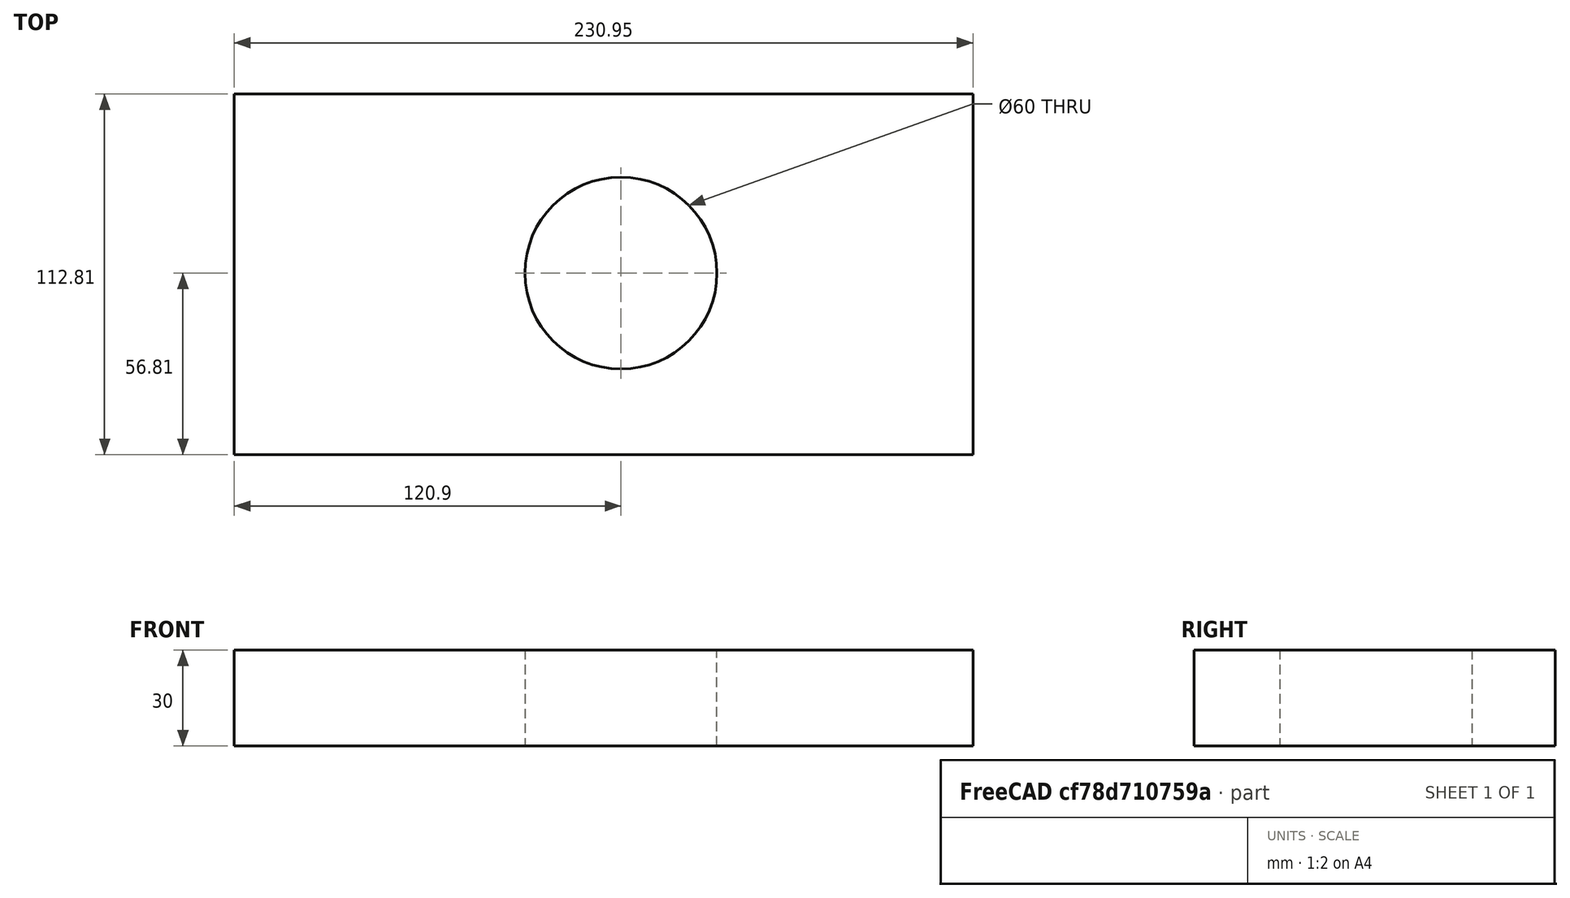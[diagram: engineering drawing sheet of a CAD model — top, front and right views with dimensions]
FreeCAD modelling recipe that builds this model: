
FCSTD DOCUMENT  (FreeCAD 0.16RUnknown)
Label: Block
License: All rights reserved
LicenseURL: http://en.wikipedia.org/wiki/All_rights_reserved
objects: Fem::FemResultObject×6, Fem::ConstraintHeatflux×2, Sketcher::SketchObject×1, PartDesign::Pad×1, Fem::FemSolverObjectPython×1, Fem::FemMeshShapeNetgenObject×1, App::MaterialObjectPython×1, Fem::ConstraintDisplacement×1, Fem::ConstraintFixed×1, Fem::ConstraintInitialTemperature×1, Fem::FemAnalysisPython×1
note: 3 computed .brp shape members not serialized (recipe doc carries the construction recipe); baked Part::Feature solids carry a one-line shape summary decoded from their .brp

FEATURE [Sketcher::SketchObject] Sketch
  sketch-geometry (5):
    g0: LineSegment StartX=-120.897 StartY=-56.8143 StartZ=0 EndX=110.046 EndY=-56.8143 EndZ=0
    g1: LineSegment StartX=110.046 StartY=-56.8143 StartZ=0 EndX=110.046 EndY=56 EndZ=0
    g2: LineSegment StartX=110.046 StartY=56 StartZ=0 EndX=-120.897 EndY=56 EndZ=0
    g3: LineSegment StartX=-120.897 StartY=56 StartZ=0 EndX=-120.897 EndY=-56.8143 EndZ=0
    g4: Circle CenterX=0 CenterY=0 CenterZ=0 NormalX=0 NormalY=0 NormalZ=1 Radius=30
  constraints (10):
    c: Coincident(g0,g1)
    c: Coincident(g1,g2)
    c: Coincident(g2,g3)
    c: Coincident(g3,g0)
    c: Horizontal(g0)
    c: Horizontal(g2)
    c: Vertical(g1)
    c: Vertical(g3)
    c: Coincident(g4,g-1)
    c: Radius(g4) = 30
FEATURE [PartDesign::Pad] Pad
  Length = 30
  Length2 = 100
  Sketch = -> Sketch
  Type = 0
FEATURE [Fem::FemSolverObjectPython] CalculiX  # FEM object (typed FeaturePython)
  AnalysisType = 2
  EigenmodeHighLimit = 1000000
  EigenmodeLowLimit = 0
  EndTime = 10
  InitialTimeStep = 1
  MatrixSolverType = 0
  Maxiterations = 2000
  NonLinearGeometry = false
  NumCpus = 3
  NumberOfEigenmodes = 10
  SolverType = FemSolverCalculix
  SteadyState = false
FEATURE [Fem::FemMeshShapeNetgenObject] Pad_Mesh
  Fineness = 3
  GrowthRate = 0.3
  MaxSize = 1000
  NbSegsPerEdge = 1
  NbSegsPerRadius = 2
  Optimize = true
  SecondOrder = true
  Shape = -> Pad
FEATURE [App::MaterialObjectPython] MechanicalMaterial  # material (typed FeaturePython)
  Material = Density=7900.0 kg/m^3,Description=Standard steel material for CalculiX sample calculations,Father=Metal,Name=CalculiX-Steel,PoissonRatio=0.3,+4 more (map truncated)
FEATURE [Fem::ConstraintDisplacement] FemConstraintDisplacement
  NormalDirection = (1,0,0)
  Normals = (32) [(1,0,0),(1,0,0),(1,0,0),(1,0,0),(1,0,0),(1,0,0),(1,0,0),(1,0,0),(1,0,0),(1,0,0),(1,0,0),(1,0,0),(1,0,0),(1,0,0),(1,0,0),(1,0,0),(-1,0,0),(-1,0,0),+14 more]
  Points = (32) [(110.046,-56.8143,30),(110.046,-19.2095,30),(110.046,18.3952,30),(110.046,56,30),(110.046,-56.8143,20),(110.046,-19.2095,20),(110.046,18.3952,20),+25 more]
  References = -> [Pad]
  Scale = 8
  rotxFix = false
  rotxFree = true
  rotyFix = false
  rotyFree = true
  rotzFix = false
  rotzFree = true
  xDisplacement = 0
  xFix = true
  xFree = false
  xRotation = 0
  yDisplacement = 0
  yFix = false
  yFree = true
  yRotation = 0
  zDisplacement = 0
  zFix = false
  zFree = true
  zRotation = 0
FEATURE [Fem::ConstraintFixed] FemConstraintFixed
  NormalDirection = (0,0,1)
  Normals = (1) [(0,0,1)]
  Points = (1) [(-120.897,56,30)]
  References = -> [Pad]
  Scale = 22
FEATURE [Fem::ConstraintHeatflux] FemConstraintHeatflux
  AmbientTemp = 300
  FilmCoef = 10
  NormalDirection = (-1,0,0)
  Normals = (16) [(-1,0,0),(-1,0,0),(-1,0,0),(-1,0,0),(-1,0,0),(-1,0,0),(-1,0,0),(-1,0,0),(-1,0,0),(-1,0,0),(-1,0,0),(-1,0,0),(-1,0,0),(-1,0,0),(-1,0,0),(-1,0,0)]
  Points = (16) [(-120.897,56,30),(-120.897,18.3952,30),(-120.897,-19.2095,30),(-120.897,-56.8143,30),(-120.897,56,20),(-120.897,18.3952,20),(-120.897,-19.2095,20),+9 more]
  References = -> [Pad]
  Scale = 8
FEATURE [Fem::ConstraintHeatflux] FemConstraintHeatflux001
  AmbientTemp = 900
  FilmCoef = 10
  NormalDirection = (1,0,0)
  Normals = (16) [(1,0,0),(1,0,0),(1,0,0),(1,0,0),(1,0,0),(1,0,0),(1,0,0),(1,0,0),(1,0,0),(1,0,0),(1,0,0),(1,0,0),(1,0,0),(1,0,0),(1,0,0),(1,0,0)]
  Points = (16) [(110.046,-56.8143,30),(110.046,-19.2095,30),(110.046,18.3952,30),(110.046,56,30),(110.046,-56.8143,20),(110.046,-19.2095,20),(110.046,18.3952,20),+9 more]
  References = -> [Pad]
  Scale = 8
FEATURE [Fem::ConstraintInitialTemperature] FemConstraintInitialTemperature
  NormalDirection = (0,0,1)
  initialTemperature = 300
FEATURE [Fem::FemResultObject] Time_1_0_results
  DisplacementLengths = [1.09043e-05,1.08621e-05,0,4.79698e-07,7.0179e-05,6.99295e-05,7.0611e-05,7.07108e-05,1.40134e-06,1.47478e-06,1.62896e-06,2.35189e-06,3.74579e-06,5.73156e-06,7.41138e-06,8.4937e-06,9.504e-06,1.14327e-05,1.50741e-05,2.118e-05,3.08816e-05,+1831 more]
  DisplacementVectors = (1852) [(-1.08695e-05,-8.70105e-07,-1.09746e-08),(-1.08346e-05,-7.69694e-07,-6.22541e-08),(0,0,0),(0,-1.00836e-08,-4.79592e-07),(0,6.18968e-05,3.30739e-05),+1847 more]
  Eigenmode = 0
  EigenmodeFrequency = 0
  MaxShear = [0.00110132,0.00145114,0.0056175,0.00559389,0.684787,0.707023,0.686506,0.593066,0.00568351,0.00566764,0.00585237,0.00650454,0.00787853,0.0090864,0.00818334,0.0068105,0.0104173,0.0157375,0.0224242,0.0399391,0.171137,0.282705,0.478545,+1829 more]
  Mesh = -> Pad_Mesh
  NodeNumbers = [1,2,3,4,5,6,7,8,9,10,11,12,13,14,15,16,17,18,19,20,21,22,23,24,25,26,27,28,29,30,31,32,33,34,35,36,37,38,39,40,41,42,43,44,45,46,47,48,49,50,51,52,53,54,55,56,57,58,59,60,61,62,63,64,65,66,67,68,69,+1783 more]
  PrincipalMax = [-5.90334e-05,0.000101181,2.19898e-05,1.62717e-05,0.850149,0.899198,0.870237,0.699655,1.6515e-05,1.54824e-05,4.15293e-05,7.79948e-05,1.57775e-05,6.37336e-05,0.000426934,0.000181857,0.00042271,0.00092082,0.00510631,0.0555829,0.198626,+1831 more]
  PrincipalMed = [-0.000244752,-0.000154764,-2.78992e-06,-3.12636e-06,0.113433,0.11918,0.0859452,0.143449,-9.03912e-06,-9.49593e-06,5.954e-06,-6.84071e-05,-6.32103e-05,-0.000156076,-0.000207615,-5.34835e-05,-0.000185036,-0.000129886,0.000802053,0.0283716,+1832 more]
  PrincipalMin = [-0.00226167,-0.00280111,-0.011213,-0.0111715,-0.519425,-0.514849,-0.502774,-0.486478,-0.0113505,-0.0113198,-0.0116632,-0.0129311,-0.0157413,-0.0181091,-0.0159397,-0.0134391,-0.0204118,-0.0305542,-0.039742,-0.0242954,-0.143649,-0.491018,+1830 more]
  Stats = [-4.08679e-05,-7.69615e-06,0,-6.38528e-05,-1.00231e-06,6.32438e-05,-4.62787e-05,-1.86336e-07,4.69683e-05,0,9.60651e-06,7.07108e-05,0.000599773,0.0453101,1.22677,-0.418726,0.0135637,0.899198,-0.615163,-0.00228516,0.40572,-1.071,-0.0358433,+4 more]
  StressValues = [0.0021159,0.00278316,0.0112226,0.0111781,1.18722,1.22677,1.19308,1.02788,0.0113543,0.0113228,0.011687,0.0129365,0.0157177,0.0180639,0.0160588,0.0135049,0.0205374,0.030963,0.0428586,0.0703377,0.316557,0.537739,0.876323,0.88264,0.764111,+1827 more]
  Temperature = [300,300,300,300,300.434,300.436,300.432,300.392,300,300,300,300,300,300,300,300,300,300,300.003,300.01,300.089,300.345,300.387,300.386,300.376,300.333,300.1,300.019,300.002,300,300,300,300,300,300,300,300,300,300,300,300,300,300,300,300,+1807 more]
  Time = 1
FEATURE [Fem::FemResultObject] Time_2_0_results
  DisplacementLengths = [2.18488e-05,2.17538e-05,0,9.58297e-07,0.00012698,0.000126633,0.000128639,0.000130319,2.79994e-06,2.95303e-06,3.25509e-06,4.70093e-06,7.48937e-06,1.14626e-05,1.48243e-05,1.699e-05,1.90122e-05,2.29244e-05,3.05133e-05,4.3104e-05,6.62821e-05,+1831 more]
  DisplacementVectors = (1852) [(-2.17801e-05,-1.72959e-06,-6.08378e-08),(-2.16977e-05,-1.55197e-06,-1.69272e-07),(0,0,0),(0,2.15053e-09,-9.58295e-07),(0,0.000113029,5.78647e-05),+1847 more]
  Eigenmode = 0
  EigenmodeFrequency = 0
  MaxShear = [0.00225657,0.00283529,0.011228,0.0111741,1.05466,1.08635,1.0603,0.939602,0.011367,0.0113247,0.0117052,0.0130111,0.0157637,0.0181787,0.0163653,0.0136216,0.0208272,0.0311753,0.0420788,0.0655236,0.231569,0.4507,0.762146,0.778937,0.649304,+1827 more]
  Mesh = -> Pad_Mesh
  NodeNumbers = <same value as first occurrence — deduplicated (x6 in doc)>
  PrincipalMax = [-0.000207255,-3.28875e-05,4.40388e-05,3.25091e-05,1.39256,1.46814,1.43479,1.19114,3.31754e-05,3.08608e-05,8.34441e-05,0.000156825,3.42952e-05,0.00012231,0.000834106,0.000354707,0.000795803,0.00104202,0.00463659,0.0547592,0.283085,0.115979,+1830 more]
  PrincipalMed = [-0.00050751,-0.000641127,-5.56256e-06,-6.27033e-06,0.159591,0.165646,0.129627,0.223159,-1.81605e-05,-1.89519e-05,1.16287e-05,-0.000138075,-0.000129735,-0.000307637,-0.000401744,-0.000107818,-0.000390272,-0.000665803,-0.00143959,0.0240729,+1832 more]
  PrincipalMin = [-0.00472039,-0.00570347,-0.0224119,-0.0223156,-0.716762,-0.704556,-0.685819,-0.68806,-0.0227009,-0.0226186,-0.023327,-0.0258654,-0.0314931,-0.0362351,-0.0318964,-0.0268885,-0.0408586,-0.0613086,-0.0795209,-0.076288,-0.180053,-0.785422,+1830 more]
  Stats = [-7.10932e-05,-1.53471e-05,0,-0.000117327,-2.00347e-06,0.00011511,-7.99931e-05,-3.91939e-07,8.11663e-05,0,1.89832e-05,0.000130319,0.0011333,0.0788371,1.89398,-0.638307,0.0235823,1.46814,-0.867213,-0.00397535,0.555405,-1.59213,-0.0621923,+4 more]
  StressValues = [0.00437075,0.00539225,0.0224312,0.0223288,1.83541,1.89398,1.85275,1.62769,0.0227085,0.0226246,0.0233746,0.0258761,0.0314457,0.0361443,0.0321304,0.0270149,0.0410742,0.0615145,0.0812899,0.118717,0.443666,0.846769,1.38725,1.42239,1.25009,+1827 more]
  Temperature = [300,300,300,300,300.664,300.665,300.661,300.618,300,300,300,300,300,300,300,300,300,300,299.999,300.001,300.057,300.569,300.614,300.616,300.607,300.553,300.068,300.003,299.999,300,300,300,300,300,300,300,300,300,300,300,300,300,300,300,300,+1807 more]
  Time = 2
FEATURE [Fem::FemResultObject] Time_3_5_results
  DisplacementLengths = [3.82841e-05,3.80991e-05,0,1.67626e-06,0.00019983,0.000199569,0.000203916,0.000207684,4.89388e-06,5.17074e-06,5.6904e-06,8.22084e-06,1.31021e-05,2.00591e-05,2.59483e-05,2.97453e-05,3.32894e-05,4.01404e-05,5.35684e-05,7.59911e-05,0.000121233,+1831 more]
  DisplacementVectors = (1852) [(-3.81667e-05,-2.9858e-06,-2.44551e-07),(-3.79979e-05,-2.74557e-06,-4.05729e-07),(0,0,0),(0,2.7475e-08,-1.67603e-06),(0,0.000180082,8.66172e-05),+1847 more]
  Eigenmode = 0
  EigenmodeFrequency = 0
  MaxShear = [0.0037116,0.00436665,0.0196363,0.0195444,1.41245,1.45008,1.42233,1.27219,0.0198882,0.0198095,0.0204815,0.0227719,0.0276033,0.0318338,0.0286527,0.023875,0.036521,0.0545377,0.0714299,0.100265,0.265172,0.603492,1.03013,1.06827,0.902574,+1827 more]
  Mesh = -> Pad_Mesh
  NodeNumbers = <same value as first occurrence — deduplicated (x6 in doc)>
  PrincipalMax = [-0.000344131,-8.16902e-06,7.73031e-05,5.68076e-05,1.99012,2.08498,2.04847,1.73146,5.845e-05,5.37905e-05,0.000147109,0.000276887,6.76441e-05,0.000202598,0.00141284,0.00061469,0.00144529,0.00141561,0.00350054,0.033374,0.356381,0.160158,+1830 more]
  PrincipalMed = [-0.000766111,-0.000807176,-9.72986e-06,-1.10015e-05,0.201287,0.206745,0.169951,0.293053,-3.19918e-05,-3.31021e-05,1.97018e-05,-0.000244848,-0.000235252,-0.000527882,-0.000669585,-0.000179093,-0.000721412,-0.00141902,-0.00458846,0.00453159,+1832 more]
  PrincipalMin = [-0.00776734,-0.00874148,-0.0391952,-0.039032,-0.834772,-0.815179,-0.796195,-0.812919,-0.039718,-0.0395652,-0.0408159,-0.0452669,-0.055139,-0.063465,-0.0558926,-0.0471353,-0.0715966,-0.10766,-0.139359,-0.167155,-0.173964,-1.04683,-1.69697,+1829 more]
  Stats = [-0.000106681,-2.67022e-05,0,-0.000188601,-3.50341e-06,0.00018259,-0.000119388,-7.37648e-07,0.000120714,0,3.27623e-05,0.000207684,0.00205536,0.119705,2.54785,-0.855803,0.0358909,2.08498,-1.04622,-0.00577115,0.670129,-2.07371,-0.0939302,+4 more]
  StressValues = [0.00722147,0.00836248,0.0392291,0.039055,2.47522,2.54785,2.50544,2.20976,0.0397313,0.0395756,0.0408995,0.0452851,0.0550559,0.0633055,0.0562931,0.0473581,0.071983,0.107686,0.138992,0.187777,0.513387,1.123,1.85958,1.93456,1.71317,1.09877,+1826 more]
  Temperature = [300,300,300,300,300.893,300.892,300.888,300.85,300,300,300,300,300,300,300,300,300,300,299.999,300,300.044,300.813,300.854,300.857,300.854,300.793,300.045,299.997,300,300,300,300,300,300,300,300,300,300,300,300,300,300,300,300,300,300,300,+1805 more]
  Time = 3.5
FEATURE [Fem::FemResultObject] Time_5_75_results
  DisplacementLengths = [6.29388e-05,6.26481e-05,0,2.75319e-06,0.000295664,0.000295775,0.000303523,0.000309661,8.02308e-06,8.48605e-06,9.33281e-06,1.34925e-05,2.15168e-05,3.29572e-05,4.26502e-05,4.89126e-05,5.47621e-05,6.60506e-05,8.82128e-05,0.000125487,+1832 more]
  DisplacementVectors = (1852) [(-6.27502e-05,-4.82071e-06,-6.80176e-07),(-6.24757e-05,-4.5684e-06,-8.40499e-07),(0,0,0),(0,5.25656e-08,-2.75269e-06),(0,0.000269929,0.000120646),+1847 more]
  Eigenmode = 0
  EigenmodeFrequency = 0
  MaxShear = [0.00498814,0.00564238,0.0322382,0.0321117,1.77884,1.81776,1.79023,1.60584,0.0326599,0.0325431,0.0336379,0.0374129,0.0453845,0.0523584,0.0471379,0.0393402,0.0601682,0.0898015,0.115688,0.16351,0.294004,0.744185,1.28713,1.35096,1.15258,+1827 more]
  Mesh = -> Pad_Mesh
  NodeNumbers = <same value as first occurrence — deduplicated (x6 in doc)>
  PrincipalMax = [-0.000468741,0.000118146,0.000127563,9.32511e-05,2.651,2.75481,2.71662,2.32596,9.6769e-05,8.81154e-05,0.000243742,0.000459558,0.000124778,0.000316176,0.00224616,0.00100294,0.00246665,0.00225985,0.00332778,0.0228985,0.456309,0.212873,+1830 more]
  PrincipalMed = [-0.00112323,-0.00103213,-1.59929e-05,-1.81313e-05,0.23893,0.242939,0.204965,0.356864,-5.29564e-05,-5.43427e-05,3.13426e-05,-0.000407813,-0.00039981,-0.000852137,-0.00104902,-0.000289348,-0.00122757,-0.00212086,-0.00788058,-0.0333792,+1832 more]
  PrincipalMin = [-0.010445,-0.0111666,-0.0643488,-0.0641301,-0.906686,-0.880708,-0.863835,-0.885721,-0.065223,-0.064998,-0.0670321,-0.0743663,-0.0906443,-0.104401,-0.0920296,-0.0776776,-0.11787,-0.177343,-0.228048,-0.304121,-0.1317,-1.2755,-2.06136,-2.1775,+1828 more]
  Stats = [-0.000155816,-4.35177e-05,0,-0.000284258,-5.75221e-06,0.000272135,-0.000167088,-1.30359e-06,0.00016798,0,5.30334e-05,0.000309661,0.00317547,0.171848,3.22406,-1.09336,0.0513149,2.75481,-1.22538,-0.00791231,0.765987,-2.53874,-0.13432,+4 more]
  StressValues = [0.00966568,0.0107559,0.0644047,0.0641678,3.14545,3.22406,3.18358,2.80501,0.0652451,0.065015,0.0671699,0.074396,0.0905079,0.104138,0.0926721,0.0780424,0.118532,0.177453,0.22598,0.302829,0.541282,1.37578,2.30545,2.42831,2.15622,1.35925,+1826 more]
  Temperature = [300,300,300,300,301.14,301.139,301.134,301.106,300,300,300,300,300,300,300,300,300,300,300,300.005,300.081,301.08,301.113,301.117,301.118,301.062,300.066,300.001,300,300,300,300,300,300,300,300,300,300,300,300,300,300,300,300,300,300,300,+1805 more]
  Time = 5.75
FEATURE [Fem::FemResultObject] Time_9_125_results
  DisplacementLengths = [9.99565e-05,9.95712e-05,0,4.36819e-06,0.000422743,0.000423581,0.000436239,0.000444834,1.26949e-05,1.34339e-05,1.4777e-05,2.13864e-05,3.41356e-05,5.23243e-05,6.776e-05,7.77691e-05,8.71183e-05,0.000105122,0.000140555,0.000200409,0.00031656,+1831 more]
  DisplacementVectors = (1852) [(-9.96614e-05,-7.51719e-06,-1.54905e-06),(-9.92888e-05,-7.34097e-06,-1.50604e-06),(0,0,0),(0,6.09043e-08,-4.36777e-06),(0,0.000390634,0.000161607),+1847 more]
  Eigenmode = 0
  EigenmodeFrequency = 0
  MaxShear = [0.00452765,0.00521802,0.0511263,0.0509801,2.15865,2.19507,2.17054,1.94849,0.051801,0.0516539,0.0533612,0.0593817,0.0721118,0.0832627,0.0750219,0.0627019,0.0957739,0.142907,0.181,0.257018,0.308981,0.872003,1.52806,1.62214,1.39436,0.853889,+1826 more]
  Mesh = -> Pad_Mesh
  NodeNumbers = <same value as first occurrence — deduplicated (x6 in doc)>
  PrincipalMax = [-0.00038728,0.000670927,0.000203634,0.000148201,3.36524,3.46907,3.43487,2.97172,0.000154879,0.000139832,0.000390405,0.000737365,0.000218659,0.000481472,0.00346453,0.00158635,0.0040173,0.00325927,0.00265183,0.0266545,0.565143,0.270433,+1830 more]
  PrincipalMed = [-0.00149438,-0.00115587,-2.5459e-05,-2.89218e-05,0.269915,0.271908,0.233694,0.41535,-8.4757e-05,-8.63912e-05,4.84774e-05,-0.00065574,-0.000652132,-0.00133589,-0.00160473,-0.000458585,-0.0019976,-0.00300538,-0.0130349,-0.0745284,0.359123,+1831 more]
  PrincipalMin = [-0.00944257,-0.0097651,-0.102049,-0.101812,-0.952064,-0.921067,-0.90621,-0.925259,-0.103447,-0.103168,-0.106332,-0.118026,-0.144005,-0.166044,-0.146579,-0.123817,-0.18753,-0.282556,-0.359349,-0.487381,-0.0528204,-1.47357,-2.39302,-2.57058,+1828 more]
  Stats = [-0.000232129,-6.83682e-05,0,-0.000412516,-9.11918e-06,0.000391762,-0.000225613,-2.20041e-06,0.000225303,0,8.28369e-05,0.000444834,0.0039013,0.240312,3.93181,-1.33043,0.07094,3.46907,-1.40025,-0.0109631,0.842995,-2.99505,-0.187863,0.391369,+3 more]
  StressValues = [0.00855563,0.00965315,0.102138,0.101872,3.85444,3.93181,3.8982,3.42919,0.103482,0.103195,0.106552,0.118073,0.14379,0.165624,0.147574,0.124394,0.188612,0.282735,0.354418,0.471656,0.544986,1.60525,2.72201,2.90144,2.57908,1.59737,0.624112,+1825 more]
  Temperature = [300,300,300,300,301.425,301.424,301.42,301.401,300,300,300,300,300,300,300,300,300,300,300.001,300.015,300.185,301.383,301.408,301.412,301.414,301.369,300.151,300.01,300,300,300,300,300,300,300,300,300,300,300,300,300,300,300,300,300,300,+1806 more]
  Time = 9.125
FEATURE [Fem::FemResultObject] Time_10_0_results
  DisplacementLengths = [0.000109557,0.000109151,0,4.7869e-06,0.000454751,0.000455776,0.000469703,0.000478871,1.3905e-05,1.47152e-05,1.61874e-05,2.34323e-05,3.74072e-05,5.73471e-05,7.42744e-05,8.52582e-05,9.55174e-05,0.000115265,0.000154153,0.000219883,0.000345919,+1831 more]
  DisplacementVectors = (1852) [(-0.000109234,-8.21328e-06,-1.78694e-06),(-0.00010884,-8.06184e-06,-1.67727e-06),(0,0,0),(0,6.12205e-08,-4.78651e-06),(0,0.000421102,0.000171672),+1847 more]
  Eigenmode = 0
  EigenmodeFrequency = 0
  MaxShear = [0.00424624,0.00495807,0.0560222,0.0558733,2.24833,2.28391,2.26029,2.02928,0.0567625,0.0566091,0.0584738,0.0650784,0.0790449,0.0912833,0.0822619,0.0687699,0.105013,0.156688,0.197882,0.280745,0.314292,0.900881,1.58294,1.68444,1.45,0.882953,+1826 more]
  Mesh = -> Pad_Mesh
  NodeNumbers = <same value as first occurrence — deduplicated (x6 in doc)>
  PrincipalMax = [-0.000347162,0.000849592,0.000223405,0.00016247,3.5353,3.63856,3.60575,3.12584,0.000169984,0.000153262,0.000428537,0.000809625,0.000243465,0.000524221,0.00377883,0.00173785,0.0044199,0.00349211,0.00247401,0.0283086,0.593549,0.284095,+1830 more]
  PrincipalMed = [-0.00157548,-0.00117106,-2.79139e-05,-3.17264e-05,0.276557,0.278067,0.239894,0.428477,-9.30244e-05,-9.47155e-05,5.29057e-05,-0.000720223,-0.000717827,-0.00146138,-0.00174835,-0.000502829,-0.00219759,-0.00323006,-0.0145134,-0.0837946,+1832 more]
  PrincipalMin = [-0.00883963,-0.00906655,-0.111821,-0.111584,-0.961351,-0.929257,-0.914839,-0.932721,-0.113355,-0.113065,-0.116519,-0.129347,-0.157846,-0.182042,-0.160745,-0.135802,-0.205606,-0.309883,-0.393289,-0.53318,-0.0350352,-1.51767,-2.46848,+1829 more]
  Stats = [-0.000251152,-7.47877e-05,0,-0.000444879,-9.99162e-06,0.000422239,-0.000240057,-2.43535e-06,0.000239409,0,9.05311e-05,0.000478871,0.00470478,0.257632,4.09972,-1.36764,0.0758925,3.63856,-1.45829,-0.011757,0.859508,-3.10141,-0.201428,+4 more]
  StressValues = [0.00794981,0.00907611,0.111919,0.11165,4.02317,4.09972,4.06805,3.57775,0.113394,0.113094,0.11676,0.129399,0.157611,0.181582,0.161831,0.136433,0.206797,0.310069,0.387549,0.514677,0.550762,1.65708,2.81702,3.01038,2.67643,1.6513,0.634153,+1825 more]
  Temperature = [300,300,300,300,301.495,301.494,301.49,301.473,300,300,300,300,300,300,300,300,300,300,300.001,300.017,300.215,301.456,301.479,301.483,301.485,301.444,300.175,300.012,300,300,300,300,300,300,300,300,300,300,300,300,300,300,300,300,300,300,+1806 more]
  Time = 10
FEATURE [Fem::FemAnalysisPython] MechanicalAnalysis  # FEM object (typed FeaturePython)
  Member = -> [CalculiX,Pad_Mesh,MechanicalMaterial,FemConstraintDisplacement,FemConstraintFixed,FemConstraintHeatflux,FemConstraintHeatflux001,FemConstraintInitialTemperature,Time_1_0_results,Time_2_0_results,Time_3_5_results,Time_5_75_results,Time_9_125_results,Time_10_0_results]
